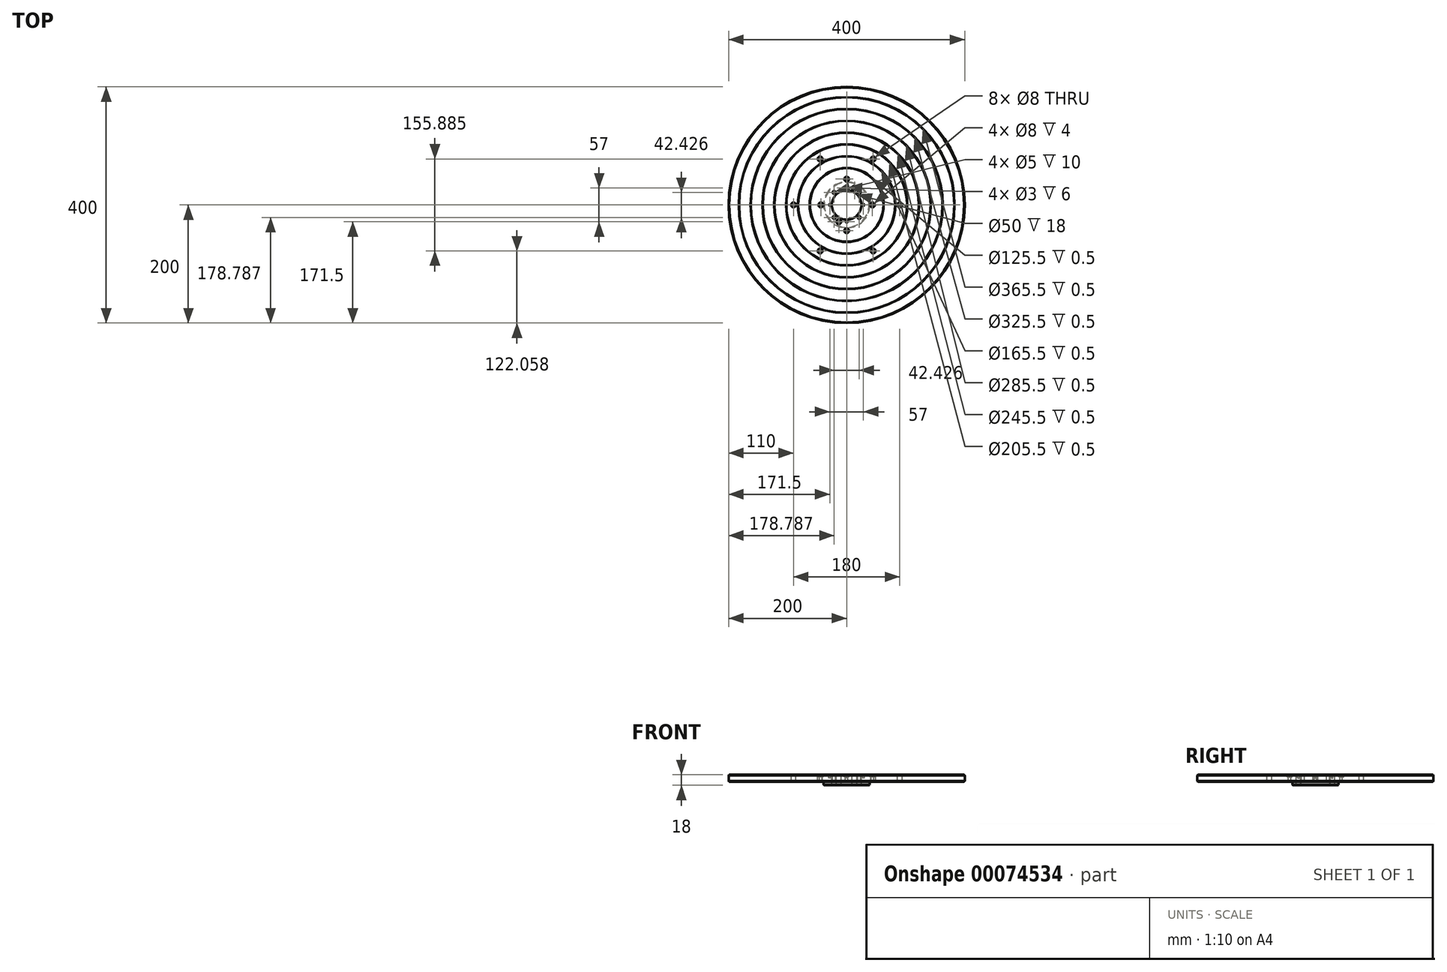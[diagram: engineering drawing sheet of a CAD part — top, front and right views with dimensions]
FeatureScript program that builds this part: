
annotation { "Feature Type Name" : "Feature", "Feature Type Description" : "" }
export const myFeature = defineFeature(function(context is Context, id is Id, definition is map)
    precondition{}
    {
        {
            var Q0;
            Q0=qCreatedBy(makeId("Top.planeOp"),FACE);
            var sketch = newSketch(context, id + "F0", { "sketchPlane" : qUnion([Q0])});
            skCircle(sketch, "E0", {"center": v(0, 0) * mm, "radius": 200 * mm});
            skSolve(sketch);
        }
        {
            var Q0;
            Q0=makeQuery(id+"F0.imprint","IMPRINT",FACE,{"disambiguationData":[TD([[makeQuery(id+"F0.imprint","IMPRINT",EDGE,{"derivedFrom":sQuery(id+"F0.wireOp",EDGE,"E0")}),1.0]])]});
            extrude(context, id + "F1", {"entities" : qUnion([Q0]), "oppositeDirection" : true, "depth" : 12 * mm});
        }
        {
            var Q0;
            Q0=makeQuery(id+"F1.opExtrude","CAP_EDGE",EDGE,{"disambiguationData":[OSD([sQuery(id+"F0.wireOp",EDGE,"E0")])],"isStart":false});
            var Q1;
            Q1=makeQuery(id+"F1.opExtrude","CAP_EDGE",EDGE,{"disambiguationData":[OSD([sQuery(id+"F0.wireOp",EDGE,"E0")])],"isStart":true});
            chamfer(context, id + "F2", {"entities" : qUnion([Q0, Q1]), "width" : 1 * mm, "tangentPropagation" : true});
        }
        {
            var Q0;
            Q0=makeQuery(id+"F1.opExtrude","CAP_FACE",FACE,{"disambiguationData":[OSD([sQuery(id+"F0.wireOp",EDGE,"E0")])],"isStart":false});
            var sketch = newSketch(context, id + "F3", { "sketchPlane" : qUnion([Q0])});
            skCircle(sketch, "E1", {"center": v(0, 0) * mm, "radius": 39 * mm});
            skSolve(sketch);
        }
        {
            var Q0;
            Q0=makeQuery(id+"F3.imprint","IMPRINT",FACE,{"disambiguationData":[TD([[makeQuery(id+"F3.imprint","IMPRINT",EDGE,{"derivedFrom":sQuery(id+"F3.wireOp",EDGE,"E1")}),1.0]])]});
            extrude(context, id + "F4", {"entities" : qUnion([Q0]), "operationType" : NewBodyOperationType.ADD, "depth" : 6 * mm});
        }
        {
            var Q0;
            Q0=makeQuery(id+"F1.opExtrude","CAP_FACE",FACE,{"disambiguationData":[OSD([sQuery(id+"F0.wireOp",EDGE,"E0")])],"isStart":true});
            var sketch = newSketch(context, id + "F5", { "sketchPlane" : qUnion([Q0])});
            skCircle(sketch, "E2", {"center": v(0, 0) * mm, "radius": 25 * mm});
            skSolve(sketch);
        }
        {
            var Q0;
            Q0=makeQuery(id+"F5.imprint","IMPRINT",FACE,{"disambiguationData":[TD([[makeQuery(id+"F5.imprint","IMPRINT",EDGE,{"derivedFrom":sQuery(id+"F5.wireOp",EDGE,"E2")}),1.0]])]});
            extrude(context, id + "F6", {"entities" : qUnion([Q0]), "operationType" : NewBodyOperationType.REMOVE, "oppositeDirection" : true, "depth" : 25 * mm});
        }
        {
            var Q0;
            Q0=makeQuery(id+"F4.opExtrude","CAP_EDGE",EDGE,{"disambiguationData":[OSD([sQuery(id+"F3.wireOp",EDGE,"E1")])],"isStart":false});
            chamfer(context, id + "F7", {"entities" : qUnion([Q0]), "width" : 1 * mm, "tangentPropagation" : true});
        }
        {
            var Q0;
            Q0=makeQuery(id+"F1.opExtrude","CAP_FACE",FACE,{"disambiguationData":[OSD([sQuery(id+"F0.wireOp",EDGE,"E0")])],"isStart":true});
            var sketch = newSketch(context, id + "F8", { "sketchPlane" : qUnion([Q0])});
            skCircle(sketch, "E3", {"center": v(0, 0) * mm, "radius": 62.25 * mm});
            skCircle(sketch, "E4", {"center": v(0, 0) * mm, "radius": 82.25 * mm});
            skCircle(sketch, "E5", {"center": v(0, 0) * mm, "radius": 102.25 * mm});
            skCircle(sketch, "E6", {"center": v(0, 0) * mm, "radius": 122.25 * mm});
            skCircle(sketch, "E7", {"center": v(0, 0) * mm, "radius": 142.25 * mm});
            skCircle(sketch, "E8", {"center": v(0, 0) * mm, "radius": 162.25 * mm});
            skCircle(sketch, "E9", {"center": v(0, 0) * mm, "radius": 182.25 * mm});
            skCircle(sketch, "E10", {"center": v(0, 0) * mm, "radius": 62.75 * mm});
            skCircle(sketch, "E11", {"center": v(0, 0) * mm, "radius": 82.75 * mm});
            skCircle(sketch, "E12", {"center": v(0, 0) * mm, "radius": 102.75 * mm});
            skCircle(sketch, "E13", {"center": v(0, 0) * mm, "radius": 122.75 * mm});
            skCircle(sketch, "E14", {"center": v(0, 0) * mm, "radius": 142.75 * mm});
            skCircle(sketch, "E15", {"center": v(0, 0) * mm, "radius": 162.75 * mm});
            skCircle(sketch, "E16", {"center": v(0, 0) * mm, "radius": 182.75 * mm});
            skSolve(sketch);
        }
        {
            var Q0;
            Q0=makeQuery(id+"F8.imprint","IMPRINT",FACE,{"disambiguationData":[TD([[makeQuery(id+"F8.imprint","IMPRINT",EDGE,{"derivedFrom":sQuery(id+"F8.wireOp",EDGE,"E3")}),-1.0]])]});
            var Q1;
            Q1=makeQuery(id+"F8.imprint","IMPRINT",FACE,{"disambiguationData":[TD([[makeQuery(id+"F8.imprint","IMPRINT",EDGE,{"derivedFrom":sQuery(id+"F8.wireOp",EDGE,"E4")}),-1.0]])]});
            var Q2;
            Q2=makeQuery(id+"F8.imprint","IMPRINT",FACE,{"disambiguationData":[TD([[makeQuery(id+"F8.imprint","IMPRINT",EDGE,{"derivedFrom":sQuery(id+"F8.wireOp",EDGE,"E5")}),-1.0]])]});
            var Q3;
            Q3=makeQuery(id+"F8.imprint","IMPRINT",FACE,{"disambiguationData":[TD([[makeQuery(id+"F8.imprint","IMPRINT",EDGE,{"derivedFrom":sQuery(id+"F8.wireOp",EDGE,"E6")}),-1.0]])]});
            var Q4;
            Q4=makeQuery(id+"F8.imprint","IMPRINT",FACE,{"disambiguationData":[TD([[makeQuery(id+"F8.imprint","IMPRINT",EDGE,{"derivedFrom":sQuery(id+"F8.wireOp",EDGE,"E7")}),-1.0]])]});
            var Q5;
            Q5=makeQuery(id+"F8.imprint","IMPRINT",FACE,{"disambiguationData":[TD([[makeQuery(id+"F8.imprint","IMPRINT",EDGE,{"derivedFrom":sQuery(id+"F8.wireOp",EDGE,"E8")}),-1.0]])]});
            var Q6;
            Q6=makeQuery(id+"F8.imprint","IMPRINT",FACE,{"disambiguationData":[TD([[makeQuery(id+"F8.imprint","IMPRINT",EDGE,{"derivedFrom":sQuery(id+"F8.wireOp",EDGE,"E9")}),-1.0]])]});
            extrude(context, id + "F9", {"entities" : qUnion([Q0, Q1, Q2, Q3, Q4, Q5, Q6]), "operationType" : NewBodyOperationType.REMOVE, "oppositeDirection" : true, "depth" : 0.5 * mm});
        }
        {
            var Q0;
            Q0=makeQuery(id+"F8.imprint","IMPRINT",FACE,{"disambiguationData":[TD([[makeQuery(id+"F8.imprint","IMPRINT",EDGE,{"derivedFrom":sQuery(id+"F8.wireOp",EDGE,"E3")}),1.0]])]});
            var sketch = newSketch(context, id + "F10", { "sketchPlane" : qUnion([Q0])});
            skCircle(sketch, "E17", {"center": v(90, 0) * mm, "radius": 4 * mm});
            skCircle(sketch, "E18.1.0", {"center": v(45, 77.94) * mm, "radius": 4 * mm});
            skCircle(sketch, "E18.2.0", {"center": v(-45, 77.94) * mm, "radius": 4 * mm});
            skCircle(sketch, "E18.3.0", {"center": v(-90, 0) * mm, "radius": 4 * mm});
            skCircle(sketch, "E18.4.0", {"center": v(-45, -77.94) * mm, "radius": 4 * mm});
            skCircle(sketch, "E18.5.0", {"center": v(45, -77.94) * mm, "radius": 4 * mm});
            skPoint(sketch, "E18.center", {"position": v(0, 0) * mm});
            skSolve(sketch);
        }
        {
            var Q0;
            Q0=makeQuery(id+"F10.imprint","IMPRINT",FACE,{"disambiguationData":[TD([[makeQuery(id+"F10.imprint","IMPRINT",EDGE,{"derivedFrom":sQuery(id+"F10.wireOp",EDGE,"E17")}),1.0]])]});
            var Q1;
            Q1=makeQuery(id+"F10.imprint","IMPRINT",FACE,{"disambiguationData":[TD([[makeQuery(id+"F10.imprint","IMPRINT",EDGE,{"derivedFrom":sQuery(id+"F10.wireOp",EDGE,"E18.1.0")}),1.0]])]});
            var Q2;
            Q2=makeQuery(id+"F10.imprint","IMPRINT",FACE,{"disambiguationData":[TD([[makeQuery(id+"F10.imprint","IMPRINT",EDGE,{"derivedFrom":sQuery(id+"F10.wireOp",EDGE,"E18.2.0")}),1.0]])]});
            var Q3;
            Q3=makeQuery(id+"F10.imprint","IMPRINT",FACE,{"disambiguationData":[TD([[makeQuery(id+"F10.imprint","IMPRINT",EDGE,{"derivedFrom":sQuery(id+"F10.wireOp",EDGE,"E18.3.0")}),1.0]])]});
            var Q4;
            Q4=makeQuery(id+"F10.imprint","IMPRINT",FACE,{"disambiguationData":[TD([[makeQuery(id+"F10.imprint","IMPRINT",EDGE,{"derivedFrom":sQuery(id+"F10.wireOp",EDGE,"E18.4.0")}),1.0]])]});
            var Q5;
            Q5=makeQuery(id+"F10.imprint","IMPRINT",FACE,{"disambiguationData":[TD([[makeQuery(id+"F10.imprint","IMPRINT",EDGE,{"derivedFrom":sQuery(id+"F10.wireOp",EDGE,"E18.5.0")}),1.0]])]});
            extrude(context, id + "F11", {"entities" : qUnion([Q0, Q1, Q2, Q3, Q4, Q5]), "operationType" : NewBodyOperationType.REMOVE, "oppositeDirection" : true, "depth" : 25 * mm});
        }
        {
            var Q0;
            Q0=makeQuery(id+"F5.imprint","IMPRINT",FACE,{"disambiguationData":[TD([[makeQuery(id+"F5.imprint","IMPRINT",EDGE,{"derivedFrom":sQuery(id+"F5.wireOp",EDGE,"E2")}),-1.0]])]});
            var sketch = newSketch(context, id + "F12", { "sketchPlane" : qUnion([Q0])});
            skCircle(sketch, "E19", {"center": v(43.75, 0) * mm, "radius": 2.1 * mm});
            skCircle(sketch, "E20", {"center": v(43.75, 0) * mm, "radius": 4 * mm});
            skCircle(sketch, "E21.1.0", {"center": v(0, 43.75) * mm, "radius": 4 * mm});
            skCircle(sketch, "E21.2.0", {"center": v(-43.75, 0) * mm, "radius": 4 * mm});
            skCircle(sketch, "E21.3.0", {"center": v(0, -43.75) * mm, "radius": 4 * mm});
            skPoint(sketch, "E21.center", {"position": v(0, 0) * mm});
            skCircle(sketch, "E22.1.0", {"center": v(0, 43.75) * mm, "radius": 2.1 * mm});
            skCircle(sketch, "E22.2.0", {"center": v(-43.75, 0) * mm, "radius": 2.1 * mm});
            skCircle(sketch, "E23.1.3.0", {"center": v(0, -43.75) * mm, "radius": 2.1 * mm});
            skCircle(sketch, "E24", {"center": v(28.5, 0) * mm, "radius": 1.5 * mm});
            skCircle(sketch, "E25.1.0", {"center": v(0, 28.5) * mm, "radius": 1.5 * mm});
            skCircle(sketch, "E25.2.0", {"center": v(-28.5, 0) * mm, "radius": 1.5 * mm});
            skCircle(sketch, "E25.3.0", {"center": v(0, -28.5) * mm, "radius": 1.5 * mm});
            skCircle(sketch, "E26", {"center": v(21.21, 21.21) * mm, "radius": 2.5 * mm});
            skLineSegment(sketch, "E27", {"start": v(0, 0) * mm, "end": v(20.12, 0) * mm, "construction": true});
            skLineSegment(sketch, "E28", {"start": v(21.21, 21.21) * mm, "end": v(0, 0) * mm, "construction": true});
            skCircle(sketch, "E29", {"center": v(13.31, 28.55) * mm, "radius": 4 * mm});
            skLineSegment(sketch, "E30", {"start": v(13.31, 28.55) * mm, "end": v(0, 0) * mm, "construction": true});
            skCircle(sketch, "E31.1.0", {"center": v(-13.31, -28.55) * mm, "radius": 4 * mm});
            skCircle(sketch, "E32.1.0", {"center": v(-21.21, 21.21) * mm, "radius": 2.5 * mm});
            skCircle(sketch, "E32.2.0", {"center": v(-21.21, -21.21) * mm, "radius": 2.5 * mm});
            skCircle(sketch, "E32.3.0", {"center": v(21.21, -21.21) * mm, "radius": 2.5 * mm});
            skSolve(sketch);
        }
        {
            var Q0;
            Q0=makeQuery(id+"F12.imprint","IMPRINT",FACE,{"disambiguationData":[TD([[makeQuery(id+"F12.imprint","IMPRINT",EDGE,{"derivedFrom":sQuery(id+"F12.wireOp",EDGE,"E22.2.0")}),1.0]])]});
            var Q1;
            Q1=makeQuery(id+"F12.imprint","IMPRINT",FACE,{"disambiguationData":[TD([[makeQuery(id+"F12.imprint","IMPRINT",EDGE,{"derivedFrom":sQuery(id+"F12.wireOp",EDGE,"E22.1.0")}),1.0]])]});
            var Q2;
            Q2=makeQuery(id+"F12.imprint","IMPRINT",FACE,{"disambiguationData":[TD([[makeQuery(id+"F12.imprint","IMPRINT",EDGE,{"derivedFrom":sQuery(id+"F12.wireOp",EDGE,"E19")}),1.0]])]});
            var Q3;
            Q3=makeQuery(id+"F12.imprint","IMPRINT",FACE,{"disambiguationData":[TD([[makeQuery(id+"F12.imprint","IMPRINT",EDGE,{"derivedFrom":sQuery(id+"F12.wireOp",EDGE,"E23.1.3.0")}),1.0]])]});
            var Q4;
            Q4=sQuery(id+"F12.wireOp",EDGE,"E22.2.0");
            extrude(context, id + "F13", {"entities" : qUnion([Q0, Q1, Q2, Q3]), "operationType" : NewBodyOperationType.REMOVE, "surfaceEntities" : qUnion([Q4]), "oppositeDirection" : true, "depth" : 25 * mm});
        }
        {
            var Q0;
            Q0=makeQuery(id+"F12.imprint","IMPRINT",FACE,{"disambiguationData":[TD([[makeQuery(id+"F12.imprint","IMPRINT",EDGE,{"derivedFrom":sQuery(id+"F12.wireOp",EDGE,"E21.2.0")}),1.0]])]});
            var Q1;
            Q1=makeQuery(id+"F12.imprint","IMPRINT",FACE,{"disambiguationData":[TD([[makeQuery(id+"F12.imprint","IMPRINT",EDGE,{"derivedFrom":sQuery(id+"F12.wireOp",EDGE,"E21.3.0")}),1.0]])]});
            var Q2;
            Q2=makeQuery(id+"F12.imprint","IMPRINT",FACE,{"disambiguationData":[TD([[makeQuery(id+"F12.imprint","IMPRINT",EDGE,{"derivedFrom":sQuery(id+"F12.wireOp",EDGE,"E19")}),-1.0]])]});
            var Q3;
            Q3=makeQuery(id+"F12.imprint","IMPRINT",FACE,{"disambiguationData":[TD([[makeQuery(id+"F12.imprint","IMPRINT",EDGE,{"derivedFrom":sQuery(id+"F12.wireOp",EDGE,"E21.1.0")}),1.0]])]});
            extrude(context, id + "F14", {"entities" : qUnion([Q0, Q1, Q2, Q3]), "operationType" : NewBodyOperationType.REMOVE, "oppositeDirection" : true, "depth" : 4 * mm});
        }
        {
            var Q0;
            Q0=makeQuery(id+"F12.imprint","IMPRINT",FACE,{"disambiguationData":[TD([[makeQuery(id+"F12.imprint","IMPRINT",EDGE,{"derivedFrom":sQuery(id+"F12.wireOp",EDGE,"E32.1.0")}),1.0]])]});
            var Q1;
            Q1=makeQuery(id+"F12.imprint","IMPRINT",FACE,{"disambiguationData":[TD([[makeQuery(id+"F12.imprint","IMPRINT",EDGE,{"derivedFrom":sQuery(id+"F12.wireOp",EDGE,"E26")}),1.0]])]});
            var Q2;
            Q2=makeQuery(id+"F12.imprint","IMPRINT",FACE,{"disambiguationData":[TD([[makeQuery(id+"F12.imprint","IMPRINT",EDGE,{"derivedFrom":sQuery(id+"F12.wireOp",EDGE,"E32.2.0")}),1.0]])]});
            var Q3;
            Q3=makeQuery(id+"F12.imprint","IMPRINT",FACE,{"disambiguationData":[TD([[makeQuery(id+"F12.imprint","IMPRINT",EDGE,{"derivedFrom":sQuery(id+"F12.wireOp",EDGE,"E32.3.0")}),1.0]])]});
            extrude(context, id + "F15", {"entities" : qUnion([Q0, Q1, Q2, Q3]), "operationType" : NewBodyOperationType.REMOVE, "oppositeDirection" : true, "depth" : 10 * mm});
        }
        {
            var Q0;
            Q0=makeQuery(id+"F12.imprint","IMPRINT",FACE,{"disambiguationData":[TD([[makeQuery(id+"F12.imprint","IMPRINT",EDGE,{"derivedFrom":sQuery(id+"F12.wireOp",EDGE,"E25.3.0")}),1.0]])]});
            var Q1;
            Q1=makeQuery(id+"F12.imprint","IMPRINT",FACE,{"disambiguationData":[TD([[makeQuery(id+"F12.imprint","IMPRINT",EDGE,{"derivedFrom":sQuery(id+"F12.wireOp",EDGE,"E24")}),1.0]])]});
            var Q2;
            Q2=makeQuery(id+"F12.imprint","IMPRINT",FACE,{"disambiguationData":[TD([[makeQuery(id+"F12.imprint","IMPRINT",EDGE,{"derivedFrom":sQuery(id+"F12.wireOp",EDGE,"E25.2.0")}),1.0]])]});
            var Q3;
            Q3=makeQuery(id+"F12.imprint","IMPRINT",FACE,{"disambiguationData":[TD([[makeQuery(id+"F12.imprint","IMPRINT",EDGE,{"derivedFrom":sQuery(id+"F12.wireOp",EDGE,"E25.1.0")}),1.0]])]});
            extrude(context, id + "F16", {"entities" : qUnion([Q0, Q1, Q2, Q3]), "operationType" : NewBodyOperationType.REMOVE, "oppositeDirection" : true, "depth" : 6 * mm});
        }
        {
            var Q0;
            Q0=makeQuery(id+"F12.imprint","IMPRINT",FACE,{"disambiguationData":[TD([[makeQuery(id+"F12.imprint","IMPRINT",EDGE,{"derivedFrom":sQuery(id+"F12.wireOp",EDGE,"E29")}),1.0]])]});
            var Q1;
            Q1=makeQuery(id+"F12.imprint","IMPRINT",FACE,{"disambiguationData":[TD([[makeQuery(id+"F12.imprint","IMPRINT",EDGE,{"derivedFrom":sQuery(id+"F12.wireOp",EDGE,"E31.1.0")}),1.0]])]});
            extrude(context, id + "F17", {"entities" : qUnion([Q0, Q1]), "operationType" : NewBodyOperationType.REMOVE, "oppositeDirection" : true, "depth" : 25 * mm});
        }
    });
